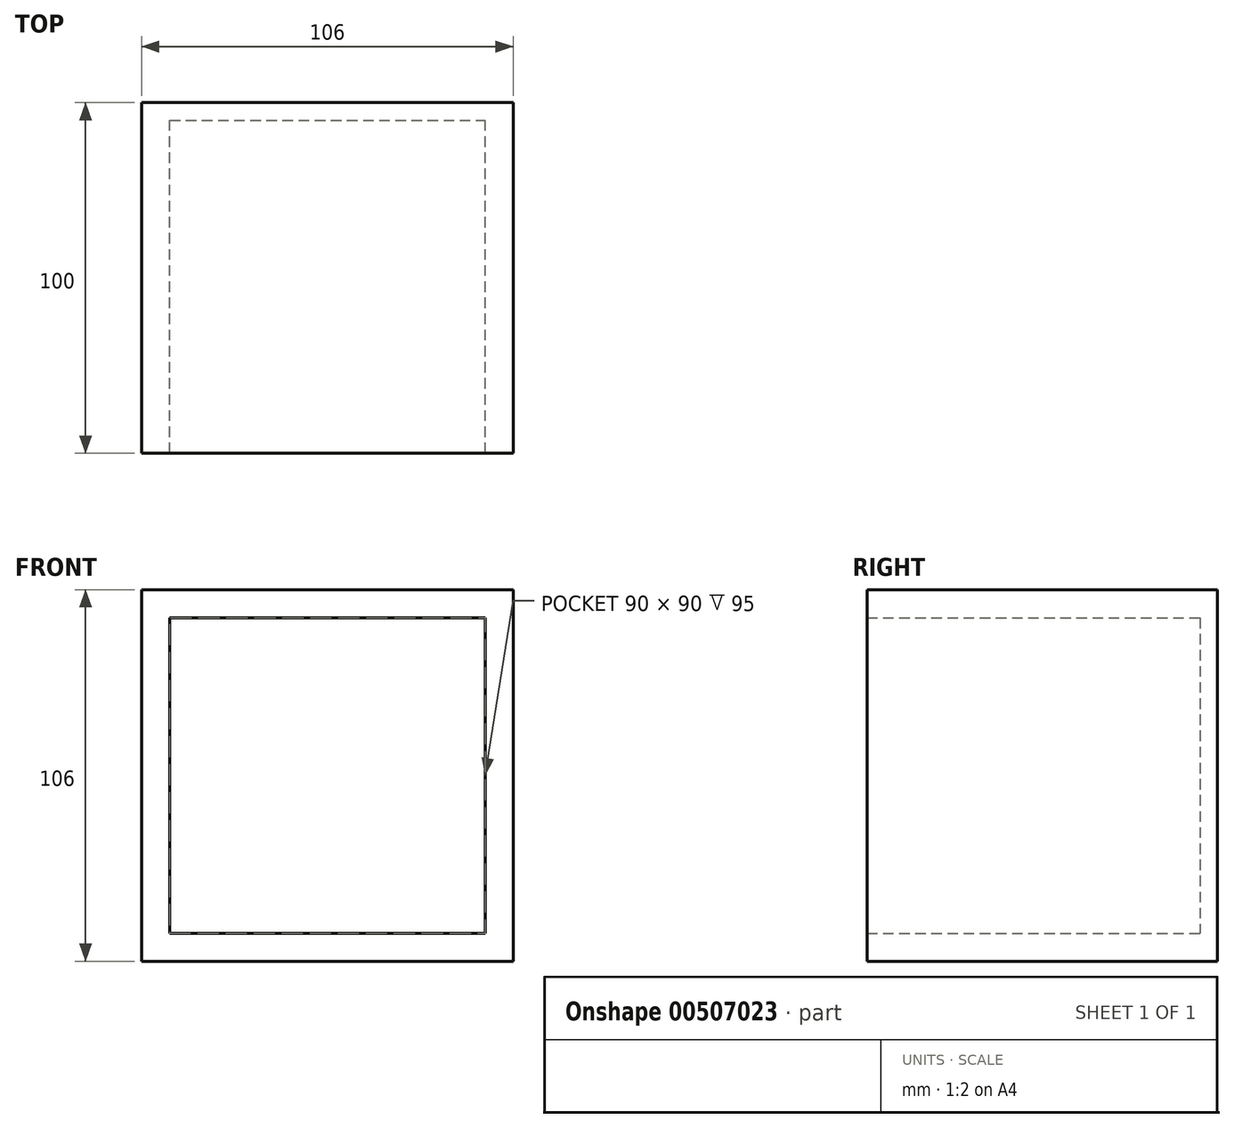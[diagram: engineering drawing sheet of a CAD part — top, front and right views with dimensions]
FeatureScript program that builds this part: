
annotation { "Feature Type Name" : "Feature", "Feature Type Description" : "" }
export const myFeature = defineFeature(function(context is Context, id is Id, definition is map)
    precondition{}
    {
        {
            var Q0;
            Q0=qCreatedBy(makeId("Front.planeOp"),FACE);
            var sketch = newSketch(context, id + "F0", { "sketchPlane" : qUnion([Q0])});
            skLineSegment(sketch, "E0.bottom", {"start": v(-43.28, 51.18) * mm, "end": v(62.72, 51.18) * mm});
            skLineSegment(sketch, "E0.top", {"start": v(-43.28, -54.82) * mm, "end": v(62.72, -54.82) * mm});
            skLineSegment(sketch, "E0.left", {"start": v(-43.28, 51.18) * mm, "end": v(-43.28, -54.82) * mm});
            skLineSegment(sketch, "E0.right", {"start": v(62.72, 51.18) * mm, "end": v(62.72, -54.82) * mm});
            skLineSegment(sketch, "E1.bottom", {"start": v(-35.28, 43.18) * mm, "end": v(54.72, 43.18) * mm});
            skLineSegment(sketch, "E1.top", {"start": v(-35.28, -46.82) * mm, "end": v(54.72, -46.82) * mm});
            skLineSegment(sketch, "E1.left", {"start": v(-35.28, 43.18) * mm, "end": v(-35.28, -46.82) * mm});
            skLineSegment(sketch, "E1.right", {"start": v(54.72, 43.18) * mm, "end": v(54.72, -46.82) * mm});
            skSolve(sketch);
        }
        {
            var Q0;
            Q0=makeQuery(id+"F0.imprint","IMPRINT",FACE,{"disambiguationData":[TD([[makeQuery(id+"F0.imprint","IMPRINT",EDGE,{"derivedFrom":sQuery(id+"F0.wireOp",EDGE,"E0.bottom")}),-1.0]])]});
            extrude(context, id + "F1", {"entities" : qUnion([Q0]), "depth" : 100 * mm, "offsetDistance" : 25 * mm});
        }
        {
            var Q0;
            Q0=makeQuery(id+"F0.imprint","IMPRINT",FACE,{"disambiguationData":[TD([[makeQuery(id+"F0.imprint","IMPRINT",EDGE,{"derivedFrom":sQuery(id+"F0.wireOp",EDGE,"E1.bottom")}),-1.0]])]});
            extrude(context, id + "F2", {"entities" : qUnion([Q0]), "operationType" : NewBodyOperationType.ADD, "depth" : 5 * mm, "offsetDistance" : 25 * mm});
        }
    });
